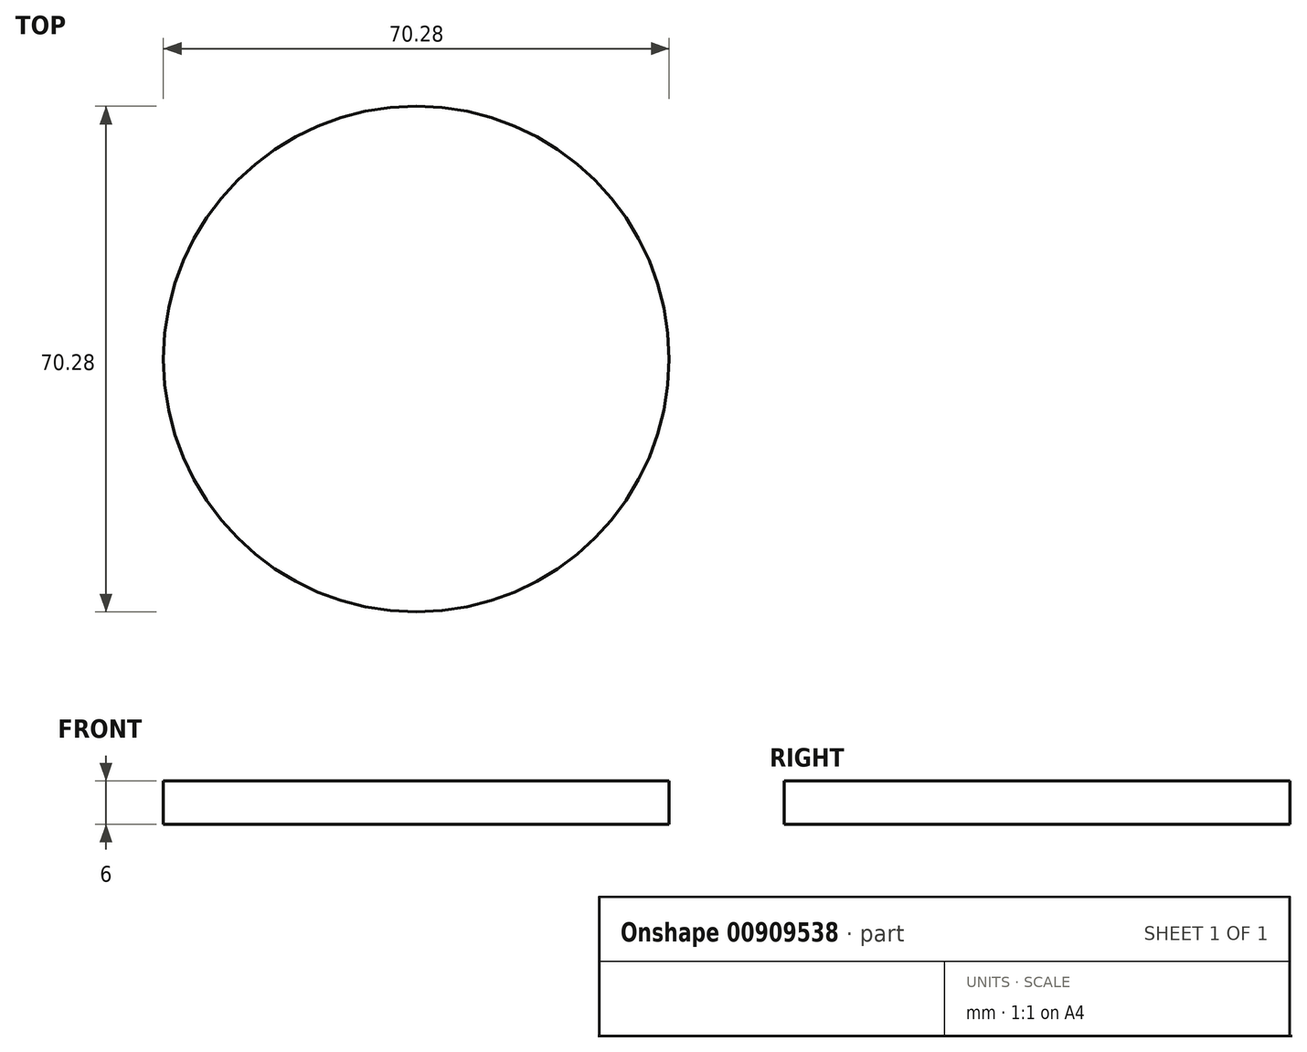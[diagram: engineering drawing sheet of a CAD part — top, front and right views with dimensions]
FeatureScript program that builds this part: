
annotation { "Feature Type Name" : "Feature", "Feature Type Description" : "" }
export const myFeature = defineFeature(function(context is Context, id is Id, definition is map)
    precondition{}
    {
        {
            var Q0;
            Q0=qCreatedBy(makeId("Top.planeOp"),FACE);
            var sketch = newSketch(context, id + "F0", { "sketchPlane" : qUnion([Q0])});
            skCircle(sketch, "E0", {"center": v(0, 0) * mm, "radius": 35.14 * mm});
            skSolve(sketch);
        }
        {
            var Q0;
            Q0 = qSketchRegion(id + "F0", true);
            extrude(context, id + "F1", {"entities" : qUnion([Q0]), "depth" : 6 * mm, "offsetDistance" : 25 * mm});
        }
    });
